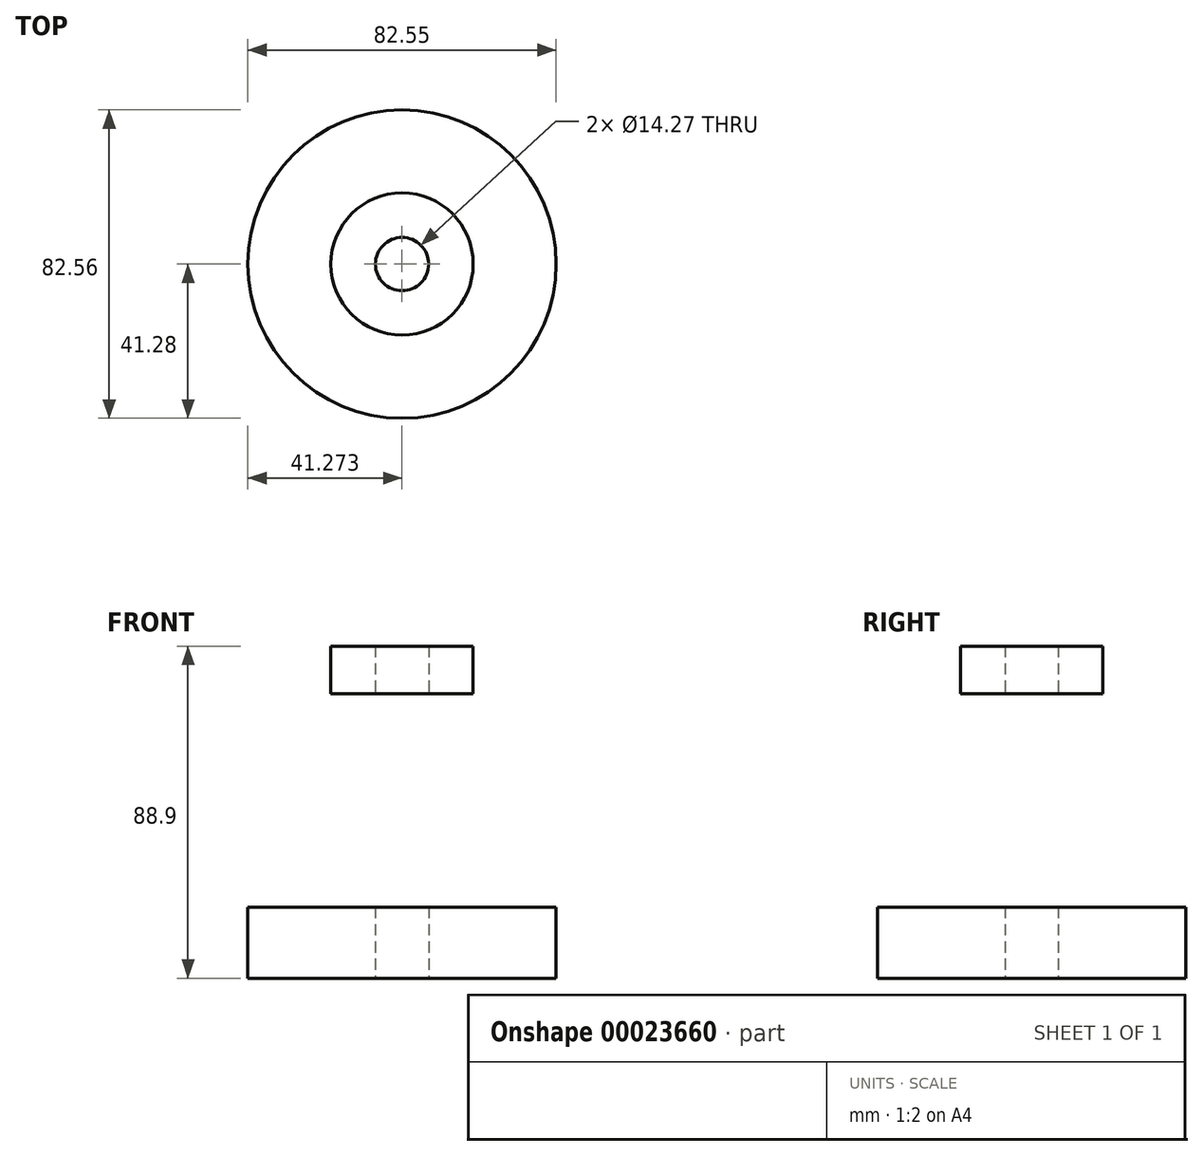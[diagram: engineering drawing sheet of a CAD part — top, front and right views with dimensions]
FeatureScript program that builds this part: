
annotation { "Feature Type Name" : "Feature", "Feature Type Description" : "" }
export const myFeature = defineFeature(function(context is Context, id is Id, definition is map)
    precondition{}
    {
        {
            var Q0;
            Q0=qCreatedBy(makeId("Front.planeOp"),FACE);
            var sketch = newSketch(context, id + "F0", { "sketchPlane" : qUnion([Q0])});
            skLineSegment(sketch, "E0", {"start": v(-11.94, 55.7) * mm, "end": v(-11.94, -33.37) * mm});
            skLineSegment(sketch, "E1.bottom", {"start": v(-11.94, 55.7) * mm, "end": v(-0.03, 55.7) * mm});
            skLineSegment(sketch, "E1.top", {"start": v(-11.94, 43) * mm, "end": v(-0.03, 43) * mm});
            skLineSegment(sketch, "E1.left", {"start": v(-11.94, 55.7) * mm, "end": v(-11.94, 43) * mm});
            skLineSegment(sketch, "E1.right", {"start": v(-0.03, 55.7) * mm, "end": v(-0.03, 43) * mm});
            skLineSegment(sketch, "E2.bottom", {"start": v(-11.94, 43) * mm, "end": v(6.32, 43) * mm});
            skLineSegment(sketch, "E2.top", {"start": v(-11.94, -14.16) * mm, "end": v(6.32, -14.16) * mm});
            skLineSegment(sketch, "E2.left", {"start": v(-11.94, 43) * mm, "end": v(-11.94, -14.16) * mm});
            skLineSegment(sketch, "E2.right", {"start": v(6.32, 43) * mm, "end": v(6.32, -14.16) * mm});
            skLineSegment(sketch, "E3.bottom", {"start": v(-11.94, -14.16) * mm, "end": v(22.2, -14.16) * mm});
            skLineSegment(sketch, "E3.top", {"start": v(-11.94, -33.2) * mm, "end": v(22.2, -33.2) * mm});
            skLineSegment(sketch, "E3.left", {"start": v(-11.94, -14.16) * mm, "end": v(-11.94, -33.2) * mm});
            skLineSegment(sketch, "E3.right", {"start": v(22.2, -14.16) * mm, "end": v(22.2, -33.2) * mm});
            skLineSegment(sketch, "E4", {"start": v(-19.08, -33.53) * mm, "end": v(-19.08, 26.89) * mm, "construction": true});
            skSolve(sketch);
        }
        {
            var Q0;
            Q0=makeQuery(id+"F0.imprint","IMPRINT",FACE,{"disambiguationData":[TD([[makeQuery(id+"F0.imprint","IMPRINT",EDGE,{"derivedFrom":sQuery(id+"F0.wireOp",EDGE,"E3.top")}),1.0]])]});
            var Q1;
            {var subQ2=sQuery(id+"F0.wireOp",EDGE,"E2.left");Q1=makeQuery(id+"F0.imprint","IMPRINT",FACE,{"disambiguationData":[TD([[makeQuery(id+"F0.imprint","IMPRINT",EDGE,{"derivedFrom":subQ2}),1.0]])]});}
            var Q2;
            Q2=makeQuery(id+"F0.imprint","IMPRINT",FACE,{"disambiguationData":[TD([[makeQuery(id+"F0.imprint","IMPRINT",EDGE,{"derivedFrom":sQuery(id+"F0.wireOp",EDGE,"E1.bottom")}),-1.0]])]});
            var Q3;
            Q3=sQuery(id+"F0.wireOp",EDGE,"E4");
            revolve(context, id + "F1", {"entities" : qUnion([Q0, Q1, Q2]), "axis" : qUnion([Q3]), "revolveType" : RevolveType.FULL});
        }
    });
